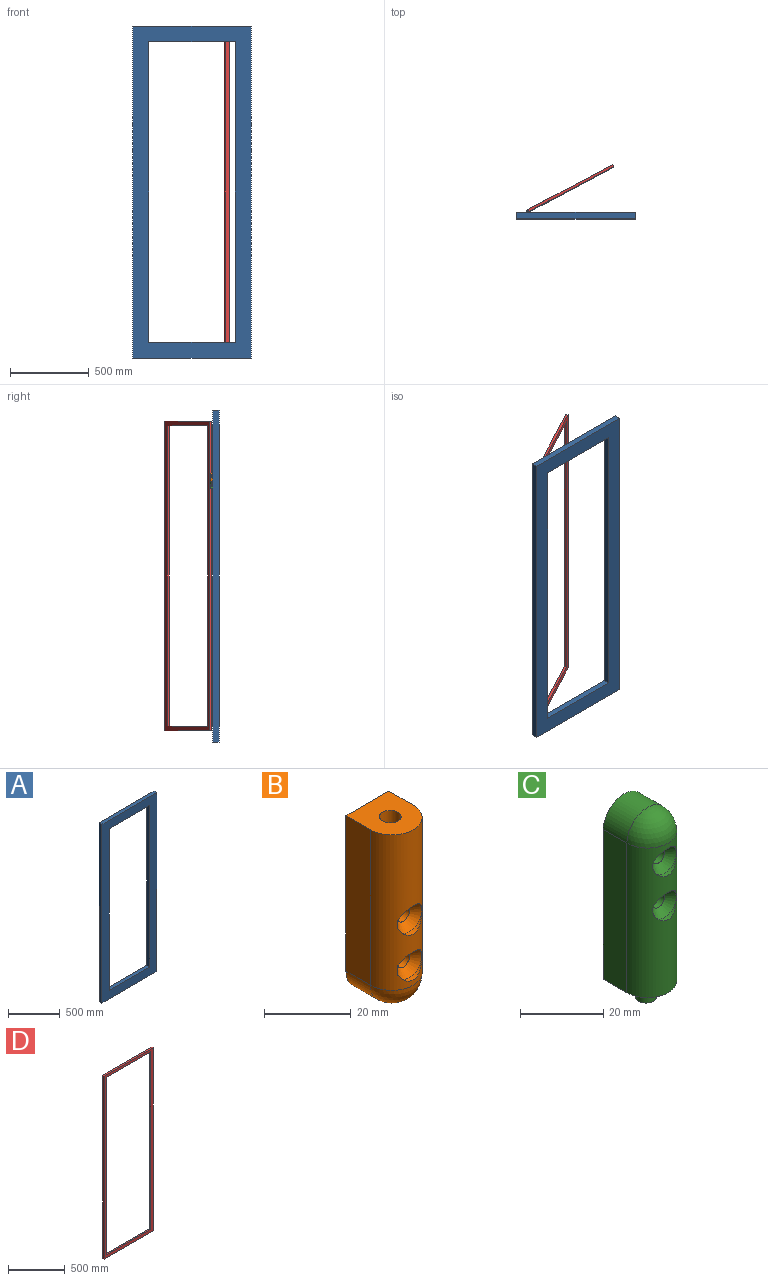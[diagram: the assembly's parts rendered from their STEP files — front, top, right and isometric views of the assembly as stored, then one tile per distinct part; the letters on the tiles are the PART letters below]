
ASSEMBLY  parts=4 mates=4
PART A: 10 faces, bbox 750x40x2110 mm
  f0: plane 2110x40mm, normal (-1,0,0), area 84400mm2, adj f2,f4,f7,f9
  f1: plane 1910x40mm, normal (1,0,0), area 76400mm2, adj f3,f5,f7,f9
  f2: plane 750x40mm, normal (0,0,-1), area 30000mm2, adj f0,f6,f7,f9
  f3: plane 550x40mm, normal (0,0,1), area 22000mm2, adj f1,f7,f8,f9
  f4: plane 750x40mm, normal (0,0,1), area 30000mm2, adj f0,f6,f7,f9
  f5: plane 550x40mm, normal (0,0,-1), area 22000mm2, adj f1,f7,f8,f9
  f6: plane 2110x40mm, normal (1,0,0), area 84400mm2, adj f2,f4,f7,f9
  f7: plane 2110x750mm, normal (0,-1,0), area 532000mm2, adj f0,f1,f2,f3,f4,f5,f6,f8
  f8: plane 1910x40mm, normal (-1,0,0), area 76400mm2, adj f3,f5,f7,f9
  f9: plane 2110x750mm, normal (0,1,0), area 532000mm2, adj f0,f1,f2,f3,f4,f5,f6,f8
PART B: 22 faces, bbox 14x15x51 mm
  f0: cylinder r=7mm len=44mm, axis (0,0,1), area 862.4mm2, adj f1,f3,f4,f6,f12,f15,f16,f19
  f1: plane 44x8mm, normal (-1,0,0), area 352mm2, adj f0,f2,f4,f5
  f2: cylinder r=7mm len=14mm, axis (0,1,0), area 175.9mm2, adj f1,f3,f5,f6
  f3: plane 44x8mm, normal (1,0,0), area 352mm2, adj f0,f2,f4,f5
  f4: plane 15x14mm, normal (0,0,1), area 169.3mm2, adj f0,f1,f3,f5,f20
  f5: plane 51x14mm, normal (0,1,0), area 178mm2, adj f1,f2,f3,f4,f7,f8,f9,f10
  f6: sphere r=7mm, area 153.9mm2, adj f0,f2
  f7: plane 42.5x2.5mm, normal (1,0,0), area 106.2mm2, adj f5,f8,f10,f11
  f8: plane 11x2.5mm, normal (0,0,-1), area 27.5mm2, adj f5,f7,f9,f11
  f9: plane 42.5x2.5mm, normal (-1,0,0), area 106.2mm2, adj f5,f8,f10,f11
  f10: cylinder r=5.5mm len=11mm, axis (0,1,0), area 43.2mm2, adj f5,f7,f9,f11
  f11: plane 48x11mm, normal (0,1,0), area 489.9mm2, adj f7,f8,f9,f10,f13,f17
  f12: cylinder r=4mm len=8mm, axis (0,-1,0), area 8.1mm2, adj f0,f14
  f13: cylinder r=2mm len=9.24mm, axis (0,-1,0), area 116.2mm2, adj f11,f14
  f14: cone r=2mm half-angle=45deg, axis (0,-1,0), area 53.3mm2, adj f12,f13,f15
  f15: cylinder r=4mm len=8mm, axis (0,-1,0), area 8.1mm2, adj f0,f14
  f16: cylinder r=4mm len=8mm, axis (0,-1,0), area 8.1mm2, adj f0,f18
  f17: cylinder r=2mm len=9.24mm, axis (0,-1,0), area 116.2mm2, adj f11,f18
  f18: cone r=2mm half-angle=45deg, axis (0,-1,0), area 53.3mm2, adj f16,f17,f19
  f19: cylinder r=4mm len=8mm, axis (0,-1,0), area 8.1mm2, adj f0,f18
  f20: cylinder r=2.5mm len=5mm, axis (0,0,-1), area 78.5mm2, adj f4,f21
  f21: plane 5x5mm, normal (0,0,1), area 19.6mm2, adj f20
PART C: 22 faces, bbox 14x15x56 mm
  f0: cylinder r=7mm len=44mm, axis (0,0,-1), area 862.4mm2, adj f1,f3,f4,f6,f12,f15,f16,f19
  f1: plane 44x8mm, normal (-1,0,0), area 352mm2, adj f0,f2,f4,f5
  f2: cylinder r=7mm len=14mm, axis (0,1,0), area 175.9mm2, adj f1,f3,f5,f6
  f3: plane 44x8mm, normal (1,0,0), area 352mm2, adj f0,f2,f4,f5
  f4: plane 15x14mm, normal (0,0,-1), area 169.3mm2, adj f0,f1,f3,f5,f20
  f5: plane 51x14mm, normal (0,1,0), area 178mm2, adj f1,f2,f3,f4,f7,f8,f9,f10
  f6: sphere r=7mm, area 153.9mm2, adj f0,f2
  f7: plane 42.5x2.5mm, normal (1,0,0), area 106.2mm2, adj f5,f8,f10,f11
  f8: plane 11x2.5mm, normal (0,0,1), area 27.5mm2, adj f5,f7,f9,f11
  f9: plane 42.5x2.5mm, normal (-1,0,0), area 106.2mm2, adj f5,f8,f10,f11
  f10: cylinder r=5.5mm len=11mm, axis (0,1,0), area 43.2mm2, adj f5,f7,f9,f11
  f11: plane 48x11mm, normal (0,1,0), area 489.9mm2, adj f7,f8,f9,f10,f13,f17
  f12: cylinder r=4mm len=8mm, axis (0,-1,0), area 8.1mm2, adj f0,f14
  f13: cylinder r=2mm len=9.24mm, axis (0,-1,0), area 116.2mm2, adj f11,f14
  f14: cone r=2mm half-angle=45deg, axis (0,-1,0), area 53.3mm2, adj f12,f13,f15
  f15: cylinder r=4mm len=8mm, axis (0,-1,0), area 8.1mm2, adj f0,f14
  f16: cylinder r=4mm len=8mm, axis (0,-1,0), area 8.1mm2, adj f0,f18
  f17: cylinder r=2mm len=9.24mm, axis (0,-1,0), area 116.2mm2, adj f11,f18
  f18: cone r=2mm half-angle=45deg, axis (0,-1,0), area 53.3mm2, adj f16,f17,f19
  f19: cylinder r=4mm len=8mm, axis (0,-1,0), area 8.1mm2, adj f0,f18
  f20: cylinder r=2.5mm len=5mm, axis (0,0,-1), area 78.5mm2, adj f4,f21
  f21: plane 5x5mm, normal (0,0,-1), area 19.6mm2, adj f20
PART D: 10 faces, bbox 610x15x1970 mm
  f0: plane 1970x15mm, normal (-1,0,0), area 29550mm2, adj f2,f4,f6,f8
  f1: plane 1910x15mm, normal (1,0,0), area 28650mm2, adj f3,f5,f6,f8
  f2: plane 610x15mm, normal (0,0,-1), area 9150mm2, adj f0,f6,f7,f8
  f3: plane 550x15mm, normal (0,0,1), area 8250mm2, adj f1,f6,f8,f9
  f4: plane 610x15mm, normal (0,0,1), area 9150mm2, adj f0,f6,f7,f8
  f5: plane 550x15mm, normal (0,0,-1), area 8250mm2, adj f1,f6,f8,f9
  f6: plane 1970x610mm, normal (0,1,0), area 151200mm2, adj f0,f1,f2,f3,f4,f5,f7,f9
  f7: plane 1970x15mm, normal (1,0,0), area 29550mm2, adj f2,f4,f6,f8
  f8: plane 1970x610mm, normal (0,-1,0), area 151200mm2, adj f0,f1,f2,f3,f4,f5,f7,f9
  f9: plane 1910x15mm, normal (-1,0,0), area 28650mm2, adj f3,f5,f6,f8
PLACE A at identity fixed
PLACE B rot(axis=(0.52,0.86,0),180deg) t=(-578.37,11.01,1558.13)mm
PLACE C rot(axis=(1,0,0),180deg) t=(-585,0,1558.13)mm fixed
PLACE D rot(axis=(0,0,-1),152.1deg) t=(-555.59,32.1,0)mm
MATE revolute B.f20 <-> C.f20  axis (0,0,-1) through (-585,7.5,1563.13)mm
MATE planar D.f5 <-> A.f5  axis (0,0,-1) through (-308.99,154.04,1910)mm
MATE planar B.f1 <-> D.f6  axis (0.47,-0.88,0) through (-582.17,1.08,1602.13)mm
MATE planar B.f2 <-> D.f7  axis (0.88,0.47,0) through (-578.37,11.01,1602.13)mm
